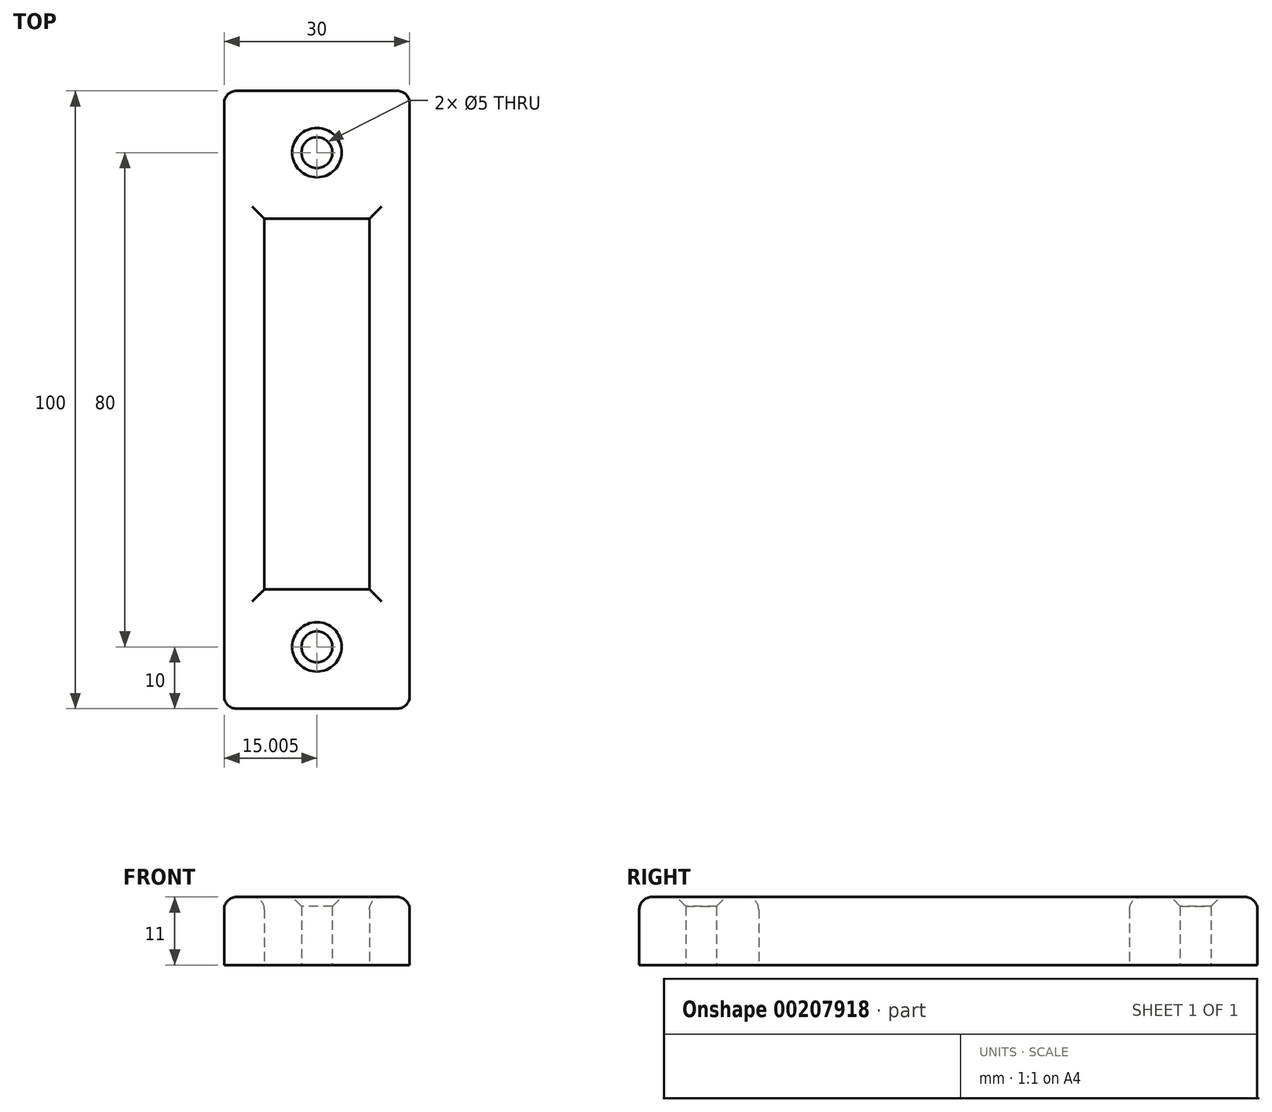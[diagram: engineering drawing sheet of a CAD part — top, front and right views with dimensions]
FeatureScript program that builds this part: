
annotation { "Feature Type Name" : "Feature", "Feature Type Description" : "" }
export const myFeature = defineFeature(function(context is Context, id is Id, definition is map)
    precondition{}
    {
        {
            var Q0;
            Q0=qCreatedBy(makeId("Top.planeOp"),FACE);
            var sketch = newSketch(context, id + "F0", { "sketchPlane" : qUnion([Q0])});
            skLineSegment(sketch, "E0.bottom", {"start": v(-9.53, 50) * mm, "end": v(20.47, 50) * mm});
            skLineSegment(sketch, "E0.top", {"start": v(-9.53, -50) * mm, "end": v(20.47, -50) * mm});
            skLineSegment(sketch, "E0.left", {"start": v(-9.53, 50) * mm, "end": v(-9.53, -50) * mm});
            skLineSegment(sketch, "E0.right", {"start": v(20.47, 50) * mm, "end": v(20.47, -50) * mm});
            skCircle(sketch, "E1", {"center": v(5.47, -40) * mm, "radius": 2.5 * mm});
            skLineSegment(sketch, "E2", {"start": v(-34.32, 0) * mm, "end": v(46.32, 0) * mm, "construction": true});
            skCircle(sketch, "E3.MirrorC", {"center": v(5.47, 40) * mm, "radius": 2.5 * mm});
            skLineSegment(sketch, "E4.bottom", {"start": v(-3.03, 29.3) * mm, "end": v(13.97, 29.3) * mm});
            skLineSegment(sketch, "E4.top", {"start": v(-3.03, -30.7) * mm, "end": v(13.97, -30.7) * mm});
            skLineSegment(sketch, "E4.left", {"start": v(-3.03, 29.3) * mm, "end": v(-3.03, -30.7) * mm});
            skLineSegment(sketch, "E4.right", {"start": v(13.97, 29.3) * mm, "end": v(13.97, -30.7) * mm});
            skSolve(sketch);
        }
        {
            var Q0;
            Q0=makeQuery(id+"F0.imprint","IMPRINT",FACE,{"disambiguationData":[TD([[makeQuery(id+"F0.imprint","IMPRINT",EDGE,{"derivedFrom":sQuery(id+"F0.wireOp",EDGE,"E0.bottom")}),-1.0]])]});
            extrude(context, id + "F1", {"entities" : qUnion([Q0]), "depth" : 11 * mm});
        }
        {
            var Q0;
            Q0=makeQuery(id+"F1.opExtrude","CAP_EDGE",EDGE,{"disambiguationData":[OSD([sQuery(id+"F0.wireOp",EDGE,"E0.bottom")])],"isStart":false});
            var Q1;
            Q1=makeQuery(id+"F1.opExtrude","CAP_EDGE",EDGE,{"disambiguationData":[OSD([sQuery(id+"F0.wireOp",EDGE,"E0.left")])],"isStart":false});
            var Q2;
            Q2=makeQuery(id+"F1.opExtrude","CAP_EDGE",EDGE,{"disambiguationData":[OSD([sQuery(id+"F0.wireOp",EDGE,"E0.right")])],"isStart":false});
            var Q3;
            Q3=makeQuery(id+"F1.opExtrude","CAP_EDGE",EDGE,{"disambiguationData":[OSD([sQuery(id+"F0.wireOp",EDGE,"E0.top")])],"isStart":false});
            var Q4;
            Q4=makeQuery(id+"F1.opExtrude","SWEPT_EDGE",EDGE,{"disambiguationData":[OSD([sQuery(id+"F0.wireOp",EDGE,"E0.top"),sQuery(id+"F0.wireOp",EDGE,"E0.left")])]});
            var Q5;
            Q5=makeQuery(id+"F1.opExtrude","SWEPT_EDGE",EDGE,{"disambiguationData":[OSD([sQuery(id+"F0.wireOp",EDGE,"E0.top"),sQuery(id+"F0.wireOp",EDGE,"E0.right")])]});
            var Q6;
            Q6=makeQuery(id+"F1.opExtrude","SWEPT_EDGE",EDGE,{"disambiguationData":[OSD([sQuery(id+"F0.wireOp",EDGE,"E0.bottom"),sQuery(id+"F0.wireOp",EDGE,"E0.left")])]});
            var Q7;
            Q7=makeQuery(id+"F1.opExtrude","SWEPT_EDGE",EDGE,{"disambiguationData":[OSD([sQuery(id+"F0.wireOp",EDGE,"E0.bottom"),sQuery(id+"F0.wireOp",EDGE,"E0.right")])]});
            var Q8;
            Q8=makeQuery(id+"F1.opExtrude","CAP_EDGE",EDGE,{"disambiguationData":[OSD([sQuery(id+"F0.wireOp",EDGE,"E4.right")])],"isStart":false});
            var Q9;
            Q9=makeQuery(id+"F1.opExtrude","CAP_EDGE",EDGE,{"disambiguationData":[OSD([sQuery(id+"F0.wireOp",EDGE,"E4.top")])],"isStart":false});
            var Q10;
            Q10=makeQuery(id+"F1.opExtrude","CAP_EDGE",EDGE,{"disambiguationData":[OSD([sQuery(id+"F0.wireOp",EDGE,"E4.left")])],"isStart":false});
            var Q11;
            Q11=makeQuery(id+"F1.opExtrude","CAP_EDGE",EDGE,{"disambiguationData":[OSD([sQuery(id+"F0.wireOp",EDGE,"E4.bottom")])],"isStart":false});
            fillet(context, id + "F2", {"entities" : qUnion([Q0, Q1, Q2, Q3, Q4, Q5, Q6, Q7, Q8, Q9, Q10, Q11]), "radius" : 2 * mm, "tangentPropagation" : true, "allowEdgeOverflow" : false});
        }
        {
            var Q0;
            Q0=makeQuery(id+"F1.opExtrude","CAP_EDGE",EDGE,{"disambiguationData":[OSD([sQuery(id+"F0.wireOp",EDGE,"E3.MirrorC")])],"isStart":false});
            var Q1;
            Q1=makeQuery(id+"F1.opExtrude","CAP_EDGE",EDGE,{"disambiguationData":[OSD([sQuery(id+"F0.wireOp",EDGE,"E1")])],"isStart":false});
            chamfer(context, id + "F3", {"entities" : qUnion([Q0, Q1]), "width" : 1.5 * mm, "tangentPropagation" : true});
        }
    });
